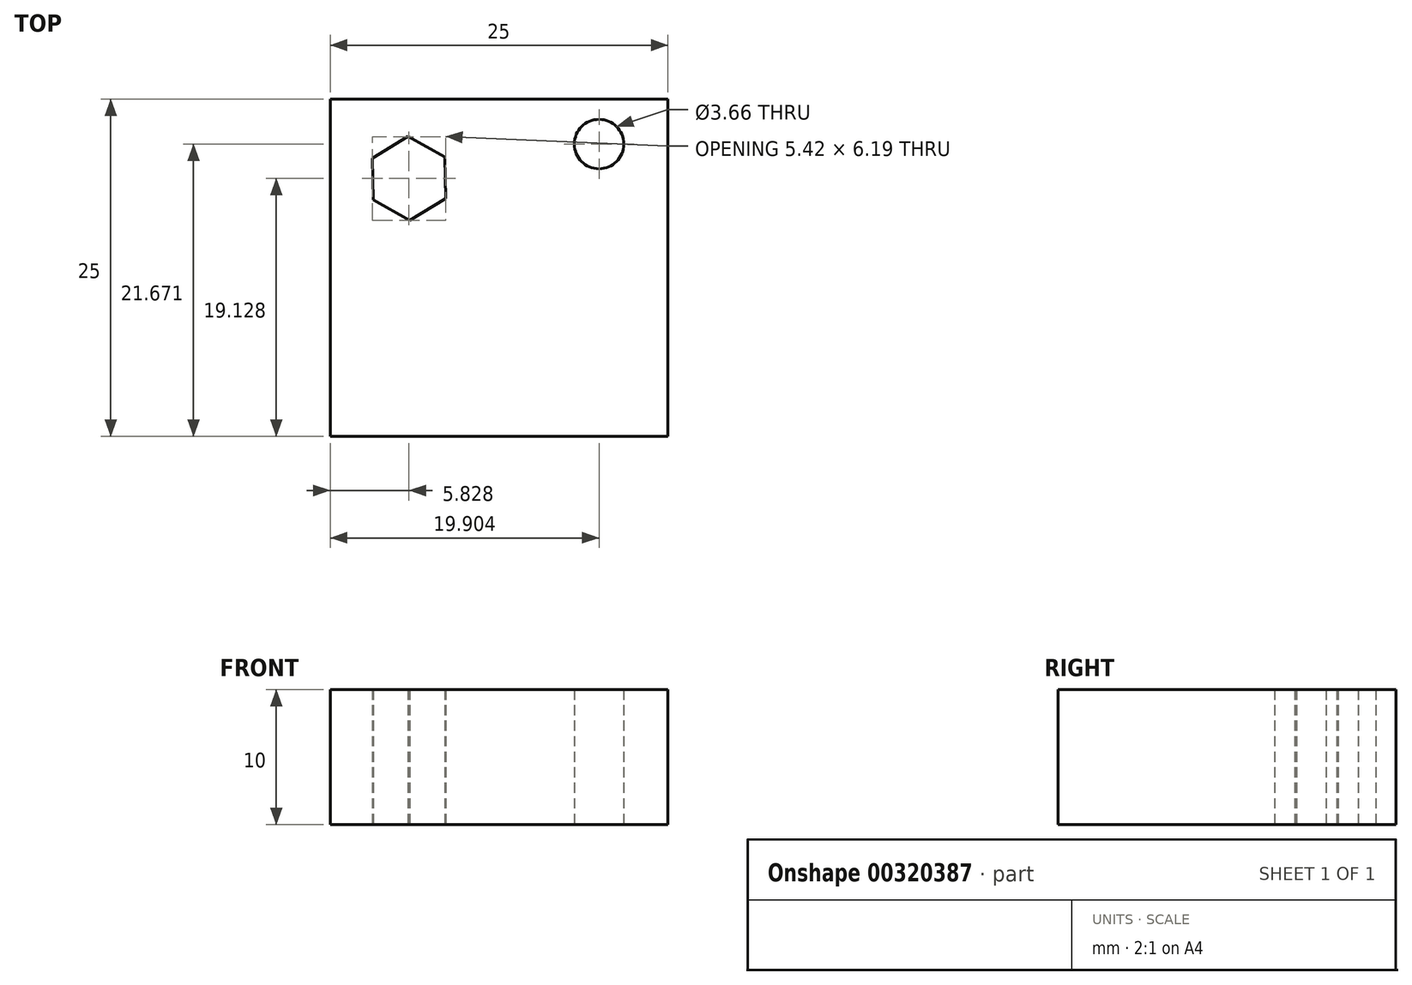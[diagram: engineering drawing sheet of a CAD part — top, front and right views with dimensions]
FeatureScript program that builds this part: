
annotation { "Feature Type Name" : "Feature", "Feature Type Description" : "" }
export const myFeature = defineFeature(function(context is Context, id is Id, definition is map)
    precondition{}
    {
        {
            var Q0;
            Q0=qCreatedBy(makeId("Top.planeOp"),FACE);
            var sketch = newSketch(context, id + "F0", { "sketchPlane" : qUnion([Q0])});
            skLineSegment(sketch, "E0.bottom", {"start": v(12.5, -12.5) * mm, "end": v(-12.5, -12.5) * mm});
            skLineSegment(sketch, "E0.top", {"start": v(12.5, 12.5) * mm, "end": v(-12.5, 12.5) * mm});
            skLineSegment(sketch, "E0.left", {"start": v(12.5, -12.5) * mm, "end": v(12.5, 12.5) * mm});
            skLineSegment(sketch, "E0.right", {"start": v(-12.5, -12.5) * mm, "end": v(-12.5, 12.5) * mm});
            skPoint(sketch, "E0.middle", {"position": v(0, 0) * mm});
            skCircle(sketch, "E1", {"center": v(7.4, 9.17) * mm, "radius": 1.83 * mm});
            skCircle(sketch, "E2.cCircle", {"center": v(-6.67, 6.63) * mm, "radius": 2.68 * mm, "construction": true});
            skLineSegment(sketch, "E2.0", {"start": v(-3.96, 5.13) * mm, "end": v(-6.61, 3.53) * mm});
            skLineSegment(sketch, "E2.1", {"start": v(-6.61, 3.53) * mm, "end": v(-9.32, 5.03) * mm});
            skLineSegment(sketch, "E2.2", {"start": v(-9.32, 5.03) * mm, "end": v(-9.38, 8.13) * mm});
            skLineSegment(sketch, "E2.3", {"start": v(-9.38, 8.13) * mm, "end": v(-6.73, 9.72) * mm});
            skLineSegment(sketch, "E2.4", {"start": v(-6.73, 9.72) * mm, "end": v(-4.02, 8.23) * mm});
            skLineSegment(sketch, "E2.5", {"start": v(-4.02, 8.23) * mm, "end": v(-3.96, 5.13) * mm});
            skPoint(sketch, "E2.0.midPoint", {"position": v(-5.29, 4.33) * mm});
            skSolve(sketch);
        }
        {
            var Q0;
            Q0 = qSketchRegion(id + "F0", true);
            extrude(context, id + "F1", {"entities" : qUnion([Q0]), "depth" : 10 * mm});
        }
    });
